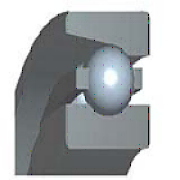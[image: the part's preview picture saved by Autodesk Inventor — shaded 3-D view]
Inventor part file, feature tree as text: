
AUTODESK INVENTOR PART (.ipt)
format: ipt  version: 2019 (Build 230136000, 136)  size: 423,936 bytes
history: native  units: mm
features: revolve x3, sketch x1, pattern_circular x1, fillet x1
ambient origin geometry x8: Origin, YZ Plane, XZ Plane, XY Plane, X Axis, Y Axis, Z Axis, Center Point
bodies: Solid1 (feature_tree)
feature tree (6):
  sketch  "Sketch1"  dims[d0=30.0mm d1=55.0mm d2=13.0mm d3=6.5mm d4=15.0deg d5=12.2mm d6=38.15mm d7=46.85mm d9=1.745329mm d10=48.59mm d11=38.15mm d12=1.745329mm d14=24.4mm d15=11.7mm d16=39.89mm d17=90.0deg d18=90.0deg d19=102.705914mm d20=360.0deg d22=0.6mm d23=1.0mm d24=45.0deg d25=45.0deg d26=90.0deg d27=0.0mm d28=0.0mm d29=0.0mm d30=0.0mm d31=0.0mm]
  revolve  "Revolution1"  [1 undecoded]
  revolve  "Revolution2"  [1 undecoded]
  pattern_circular  "Circular Pattern1"  [2 undecoded]
  fillet  "Fillet1"  [1 undecoded]
  revolve  "Revolution3"  [1 undecoded]
note: 6 required parameter values undecoded (feature->parameter linkage not recoverable at this tier; creation-order binding heuristic only, values carry confidence <= 0.55)